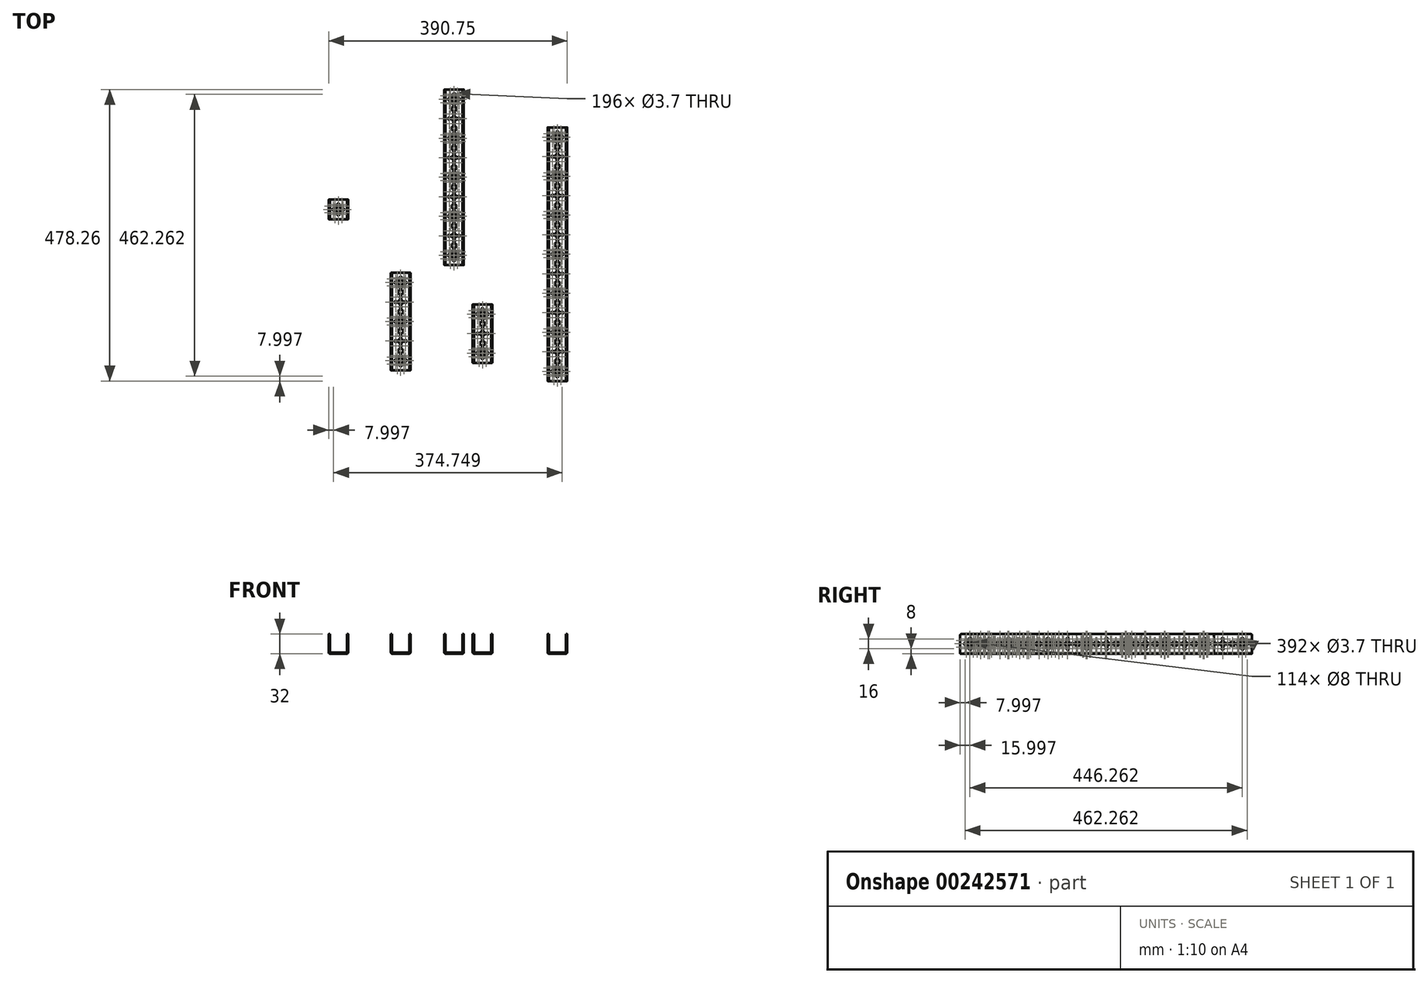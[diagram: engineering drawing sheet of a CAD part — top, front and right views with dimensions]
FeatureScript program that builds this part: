
annotation { "Feature Type Name" : "Feature", "Feature Type Description" : "" }
export const myFeature = defineFeature(function(context is Context, id is Id, definition is map)
    precondition{}
    {
        {
            var Q0;
            Q0=qCreatedBy(makeId("Top.planeOp"),FACE);
            var sketch = newSketch(context, id + "F0", { "sketchPlane" : qUnion([Q0])});
            skLineSegment(sketch, "E0.bottom", {"start": v(-59.46, 42.92) * mm, "end": v(-27.46, 42.92) * mm});
            skLineSegment(sketch, "E0.top", {"start": v(-59.46, -53.08) * mm, "end": v(-27.46, -53.08) * mm});
            skLineSegment(sketch, "E0.left", {"start": v(-59.46, 42.92) * mm, "end": v(-59.46, -53.08) * mm});
            skLineSegment(sketch, "E0.right", {"start": v(-27.46, 42.92) * mm, "end": v(-27.46, -53.08) * mm});
            skCircle(sketch, "E1", {"center": v(-43.46, 26.92) * mm, "radius": 4 * mm});
            skCircle(sketch, "E2.0.1.0", {"center": v(-43.46, 10.92) * mm, "radius": 4 * mm});
            skCircle(sketch, "E2.0.2.0", {"center": v(-43.46, -5.08) * mm, "radius": 4 * mm});
            skCircle(sketch, "E2.0.3.0", {"center": v(-43.46, -21.08) * mm, "radius": 4 * mm});
            skCircle(sketch, "E2.0.4.0", {"center": v(-43.46, -37.08) * mm, "radius": 4 * mm});
            skLineSegment(sketch, "E2.direction1", {"start": v(-43.46, 26.92) * mm, "end": v(4.3, 26.92) * mm, "construction": true});
            skLineSegment(sketch, "E2.direction2", {"start": v(-43.46, 26.92) * mm, "end": v(-43.46, 10.92) * mm, "construction": true});
            skCircle(sketch, "E3", {"center": v(-43.46, 34.92) * mm, "radius": 1.85 * mm});
            skCircle(sketch, "E4.1.0", {"center": v(-49.12, 32.57) * mm, "radius": 1.85 * mm});
            skCircle(sketch, "E4.2.0", {"center": v(-51.46, 26.92) * mm, "radius": 1.85 * mm});
            skCircle(sketch, "E4.3.0", {"center": v(-49.12, 21.26) * mm, "radius": 1.85 * mm});
            skCircle(sketch, "E4.4.0", {"center": v(-43.46, 18.92) * mm, "radius": 1.85 * mm});
            skCircle(sketch, "E4.5.0", {"center": v(-37.8, 21.26) * mm, "radius": 1.85 * mm});
            skCircle(sketch, "E4.6.0", {"center": v(-35.46, 26.92) * mm, "radius": 1.85 * mm});
            skCircle(sketch, "E4.7.0", {"center": v(-37.8, 32.57) * mm, "radius": 1.85 * mm});
            skCircle(sketch, "E5.0.1.0", {"center": v(-43.46, -13.08) * mm, "radius": 1.85 * mm});
            skCircle(sketch, "E5.0.1.1", {"center": v(-51.46, -5.08) * mm, "radius": 1.85 * mm});
            skCircle(sketch, "E5.0.1.2", {"center": v(-43.46, 2.92) * mm, "radius": 1.85 * mm});
            skCircle(sketch, "E5.0.1.3", {"center": v(-35.46, -5.08) * mm, "radius": 1.85 * mm});
            skCircle(sketch, "E5.0.2.0", {"center": v(-43.46, -45.08) * mm, "radius": 1.85 * mm});
            skCircle(sketch, "E5.0.2.1", {"center": v(-51.46, -37.08) * mm, "radius": 1.85 * mm});
            skCircle(sketch, "E5.0.2.2", {"center": v(-43.46, -29.08) * mm, "radius": 1.85 * mm});
            skCircle(sketch, "E5.0.2.3", {"center": v(-35.46, -37.08) * mm, "radius": 1.85 * mm});
            skCircle(sketch, "E5.0.2.4", {"center": v(-37.8, -42.74) * mm, "radius": 1.85 * mm});
            skCircle(sketch, "E5.0.2.5", {"center": v(-49.12, -42.74) * mm, "radius": 1.85 * mm});
            skCircle(sketch, "E5.0.2.6", {"center": v(-49.12, -31.43) * mm, "radius": 1.85 * mm});
            skCircle(sketch, "E5.0.2.7", {"center": v(-37.8, -31.43) * mm, "radius": 1.85 * mm});
            skLineSegment(sketch, "E5.direction1", {"start": v(-43.46, 18.92) * mm, "end": v(-18.06, 18.92) * mm, "construction": true});
            skLineSegment(sketch, "E5.direction2", {"start": v(-43.46, 18.92) * mm, "end": v(-43.46, -13.08) * mm, "construction": true});
            skLineSegment(sketch, "E6.bottom", {"start": v(63.23, 333.14) * mm, "end": v(95.23, 333.14) * mm});
            skLineSegment(sketch, "E6.top", {"start": v(63.23, -82.86) * mm, "end": v(95.23, -82.86) * mm});
            skLineSegment(sketch, "E6.left", {"start": v(63.23, 333.14) * mm, "end": v(63.23, -82.86) * mm});
            skLineSegment(sketch, "E6.right", {"start": v(95.23, 333.14) * mm, "end": v(95.23, -82.86) * mm});
            skCircle(sketch, "E7", {"center": v(79.23, -66.86) * mm, "radius": 4 * mm});
            skCircle(sketch, "E8.0.1.0", {"center": v(79.23, -50.86) * mm, "radius": 4 * mm});
            skCircle(sketch, "E8.0.2.0", {"center": v(79.23, -34.86) * mm, "radius": 4 * mm});
            skCircle(sketch, "E8.0.3.0", {"center": v(79.23, -18.86) * mm, "radius": 4 * mm});
            skCircle(sketch, "E8.0.4.0", {"center": v(79.23, -2.86) * mm, "radius": 4 * mm});
            skCircle(sketch, "E8.0.5.0", {"center": v(79.23, 13.14) * mm, "radius": 4 * mm});
            skCircle(sketch, "E8.0.6.0", {"center": v(79.23, 29.14) * mm, "radius": 4 * mm});
            skCircle(sketch, "E8.0.7.0", {"center": v(79.23, 45.14) * mm, "radius": 4 * mm});
            skCircle(sketch, "E8.0.8.0", {"center": v(79.23, 61.14) * mm, "radius": 4 * mm});
            skCircle(sketch, "E8.0.9.0", {"center": v(79.23, 77.14) * mm, "radius": 4 * mm});
            skCircle(sketch, "E8.0.10.0", {"center": v(79.23, 93.14) * mm, "radius": 4 * mm});
            skCircle(sketch, "E8.0.11.0", {"center": v(79.23, 109.14) * mm, "radius": 4 * mm});
            skCircle(sketch, "E8.0.12.0", {"center": v(79.23, 125.14) * mm, "radius": 4 * mm});
            skCircle(sketch, "E8.0.13.0", {"center": v(79.23, 141.14) * mm, "radius": 4 * mm});
            skCircle(sketch, "E8.0.14.0", {"center": v(79.23, 157.14) * mm, "radius": 4 * mm});
            skCircle(sketch, "E8.0.15.0", {"center": v(79.23, 173.14) * mm, "radius": 4 * mm});
            skCircle(sketch, "E8.0.16.0", {"center": v(79.23, 189.14) * mm, "radius": 4 * mm});
            skCircle(sketch, "E8.0.17.0", {"center": v(79.23, 205.14) * mm, "radius": 4 * mm});
            skCircle(sketch, "E8.0.18.0", {"center": v(79.23, 221.14) * mm, "radius": 4 * mm});
            skCircle(sketch, "E8.0.19.0", {"center": v(79.23, 237.14) * mm, "radius": 4 * mm});
            skCircle(sketch, "E8.0.20.0", {"center": v(79.23, 253.14) * mm, "radius": 4 * mm});
            skCircle(sketch, "E8.0.21.0", {"center": v(79.23, 269.14) * mm, "radius": 4 * mm});
            skCircle(sketch, "E8.0.22.0", {"center": v(79.23, 285.14) * mm, "radius": 4 * mm});
            skCircle(sketch, "E8.0.23.0", {"center": v(79.23, 301.14) * mm, "radius": 4 * mm});
            skCircle(sketch, "E8.0.24.0", {"center": v(79.23, 317.14) * mm, "radius": 4 * mm});
            skLineSegment(sketch, "E8.direction1", {"start": v(79.23, -66.86) * mm, "end": v(104.63, -66.86) * mm, "construction": true});
            skLineSegment(sketch, "E8.direction2", {"start": v(79.23, -66.86) * mm, "end": v(79.23, -50.86) * mm, "construction": true});
            skCircle(sketch, "E9", {"center": v(79.23, -74.86) * mm, "radius": 1.85 * mm});
            skCircle(sketch, "E10.1.0", {"center": v(84.88, -72.52) * mm, "radius": 1.85 * mm});
            skCircle(sketch, "E10.2.0", {"center": v(87.23, -66.86) * mm, "radius": 1.85 * mm});
            skCircle(sketch, "E10.3.0", {"center": v(84.88, -61.2) * mm, "radius": 1.85 * mm});
            skCircle(sketch, "E10.4.0", {"center": v(79.23, -58.86) * mm, "radius": 1.85 * mm});
            skCircle(sketch, "E10.5.0", {"center": v(73.57, -61.2) * mm, "radius": 1.85 * mm});
            skCircle(sketch, "E10.6.0", {"center": v(71.23, -66.86) * mm, "radius": 1.85 * mm});
            skCircle(sketch, "E10.7.0", {"center": v(73.57, -72.52) * mm, "radius": 1.85 * mm});
            skCircle(sketch, "E11.0.1.0", {"center": v(79.23, -26.86) * mm, "radius": 1.85 * mm});
            skCircle(sketch, "E11.0.1.2", {"center": v(71.23, -34.86) * mm, "radius": 1.85 * mm});
            skCircle(sketch, "E11.0.1.4", {"center": v(79.23, -42.86) * mm, "radius": 1.85 * mm});
            skCircle(sketch, "E11.0.1.6", {"center": v(87.23, -34.86) * mm, "radius": 1.85 * mm});
            skCircle(sketch, "E11.0.2.0", {"center": v(79.23, 5.14) * mm, "radius": 1.85 * mm});
            skCircle(sketch, "E11.0.2.1", {"center": v(73.57, 2.8) * mm, "radius": 1.85 * mm});
            skCircle(sketch, "E11.0.2.2", {"center": v(71.23, -2.86) * mm, "radius": 1.85 * mm});
            skCircle(sketch, "E11.0.2.3", {"center": v(73.57, -8.52) * mm, "radius": 1.85 * mm});
            skCircle(sketch, "E11.0.2.4", {"center": v(79.23, -10.86) * mm, "radius": 1.85 * mm});
            skCircle(sketch, "E11.0.2.5", {"center": v(84.88, -8.52) * mm, "radius": 1.85 * mm});
            skCircle(sketch, "E11.0.2.6", {"center": v(87.23, -2.86) * mm, "radius": 1.85 * mm});
            skCircle(sketch, "E11.0.2.7", {"center": v(84.88, 2.8) * mm, "radius": 1.85 * mm});
            skCircle(sketch, "E11.0.3.0", {"center": v(79.23, 37.14) * mm, "radius": 1.85 * mm});
            skCircle(sketch, "E11.0.3.2", {"center": v(71.23, 29.14) * mm, "radius": 1.85 * mm});
            skCircle(sketch, "E11.0.3.4", {"center": v(79.23, 21.14) * mm, "radius": 1.85 * mm});
            skCircle(sketch, "E11.0.3.6", {"center": v(87.23, 29.14) * mm, "radius": 1.85 * mm});
            skCircle(sketch, "E11.0.4.0", {"center": v(79.23, 69.14) * mm, "radius": 1.85 * mm});
            skCircle(sketch, "E11.0.4.1", {"center": v(73.57, 66.8) * mm, "radius": 1.85 * mm});
            skCircle(sketch, "E11.0.4.2", {"center": v(71.23, 61.14) * mm, "radius": 1.85 * mm});
            skCircle(sketch, "E11.0.4.3", {"center": v(73.57, 55.48) * mm, "radius": 1.85 * mm});
            skCircle(sketch, "E11.0.4.4", {"center": v(79.23, 53.14) * mm, "radius": 1.85 * mm});
            skCircle(sketch, "E11.0.4.5", {"center": v(84.88, 55.48) * mm, "radius": 1.85 * mm});
            skCircle(sketch, "E11.0.4.6", {"center": v(87.23, 61.14) * mm, "radius": 1.85 * mm});
            skCircle(sketch, "E11.0.4.7", {"center": v(84.88, 66.8) * mm, "radius": 1.85 * mm});
            skCircle(sketch, "E11.0.5.0", {"center": v(79.23, 101.14) * mm, "radius": 1.85 * mm});
            skCircle(sketch, "E11.0.5.2", {"center": v(71.23, 93.14) * mm, "radius": 1.85 * mm});
            skCircle(sketch, "E11.0.5.4", {"center": v(79.23, 85.14) * mm, "radius": 1.85 * mm});
            skCircle(sketch, "E11.0.5.6", {"center": v(87.23, 93.14) * mm, "radius": 1.85 * mm});
            skCircle(sketch, "E11.0.6.0", {"center": v(79.23, 133.14) * mm, "radius": 1.85 * mm});
            skCircle(sketch, "E11.0.6.1", {"center": v(73.57, 130.8) * mm, "radius": 1.85 * mm});
            skCircle(sketch, "E11.0.6.2", {"center": v(71.23, 125.14) * mm, "radius": 1.85 * mm});
            skCircle(sketch, "E11.0.6.3", {"center": v(73.57, 119.48) * mm, "radius": 1.85 * mm});
            skCircle(sketch, "E11.0.6.4", {"center": v(79.23, 117.14) * mm, "radius": 1.85 * mm});
            skCircle(sketch, "E11.0.6.5", {"center": v(84.88, 119.48) * mm, "radius": 1.85 * mm});
            skCircle(sketch, "E11.0.6.6", {"center": v(87.23, 125.14) * mm, "radius": 1.85 * mm});
            skCircle(sketch, "E11.0.6.7", {"center": v(84.88, 130.8) * mm, "radius": 1.85 * mm});
            skCircle(sketch, "E11.0.7.0", {"center": v(79.23, 165.14) * mm, "radius": 1.85 * mm});
            skCircle(sketch, "E11.0.7.2", {"center": v(71.23, 157.14) * mm, "radius": 1.85 * mm});
            skCircle(sketch, "E11.0.7.4", {"center": v(79.23, 149.14) * mm, "radius": 1.85 * mm});
            skCircle(sketch, "E11.0.7.6", {"center": v(87.23, 157.14) * mm, "radius": 1.85 * mm});
            skCircle(sketch, "E11.0.8.0", {"center": v(79.23, 197.14) * mm, "radius": 1.85 * mm});
            skCircle(sketch, "E11.0.8.1", {"center": v(73.57, 194.8) * mm, "radius": 1.85 * mm});
            skCircle(sketch, "E11.0.8.2", {"center": v(71.23, 189.14) * mm, "radius": 1.85 * mm});
            skCircle(sketch, "E11.0.8.3", {"center": v(73.57, 183.48) * mm, "radius": 1.85 * mm});
            skCircle(sketch, "E11.0.8.4", {"center": v(79.23, 181.14) * mm, "radius": 1.85 * mm});
            skCircle(sketch, "E11.0.8.5", {"center": v(84.88, 183.48) * mm, "radius": 1.85 * mm});
            skCircle(sketch, "E11.0.8.6", {"center": v(87.23, 189.14) * mm, "radius": 1.85 * mm});
            skCircle(sketch, "E11.0.8.7", {"center": v(84.88, 194.8) * mm, "radius": 1.85 * mm});
            skCircle(sketch, "E11.0.9.0", {"center": v(79.23, 229.14) * mm, "radius": 1.85 * mm});
            skCircle(sketch, "E11.0.9.2", {"center": v(71.23, 221.14) * mm, "radius": 1.85 * mm});
            skCircle(sketch, "E11.0.9.4", {"center": v(79.23, 213.14) * mm, "radius": 1.85 * mm});
            skCircle(sketch, "E11.0.9.6", {"center": v(87.23, 221.14) * mm, "radius": 1.85 * mm});
            skCircle(sketch, "E11.0.10.0", {"center": v(79.23, 261.14) * mm, "radius": 1.85 * mm});
            skCircle(sketch, "E11.0.10.1", {"center": v(73.57, 258.8) * mm, "radius": 1.85 * mm});
            skCircle(sketch, "E11.0.10.2", {"center": v(71.23, 253.14) * mm, "radius": 1.85 * mm});
            skCircle(sketch, "E11.0.10.3", {"center": v(73.57, 247.48) * mm, "radius": 1.85 * mm});
            skCircle(sketch, "E11.0.10.4", {"center": v(79.23, 245.14) * mm, "radius": 1.85 * mm});
            skCircle(sketch, "E11.0.10.5", {"center": v(84.88, 247.48) * mm, "radius": 1.85 * mm});
            skCircle(sketch, "E11.0.10.6", {"center": v(87.23, 253.14) * mm, "radius": 1.85 * mm});
            skCircle(sketch, "E11.0.10.7", {"center": v(84.88, 258.8) * mm, "radius": 1.85 * mm});
            skCircle(sketch, "E11.0.11.0", {"center": v(79.23, 293.14) * mm, "radius": 1.85 * mm});
            skCircle(sketch, "E11.0.11.2", {"center": v(71.23, 285.14) * mm, "radius": 1.85 * mm});
            skCircle(sketch, "E11.0.11.4", {"center": v(79.23, 277.14) * mm, "radius": 1.85 * mm});
            skCircle(sketch, "E11.0.11.6", {"center": v(87.23, 285.14) * mm, "radius": 1.85 * mm});
            skCircle(sketch, "E11.0.12.0", {"center": v(79.23, 325.14) * mm, "radius": 1.85 * mm});
            skCircle(sketch, "E11.0.12.1", {"center": v(73.57, 322.8) * mm, "radius": 1.85 * mm});
            skCircle(sketch, "E11.0.12.2", {"center": v(71.23, 317.14) * mm, "radius": 1.85 * mm});
            skCircle(sketch, "E11.0.12.3", {"center": v(73.57, 311.48) * mm, "radius": 1.85 * mm});
            skCircle(sketch, "E11.0.12.4", {"center": v(79.23, 309.14) * mm, "radius": 1.85 * mm});
            skCircle(sketch, "E11.0.12.5", {"center": v(84.88, 311.48) * mm, "radius": 1.85 * mm});
            skCircle(sketch, "E11.0.12.6", {"center": v(87.23, 317.14) * mm, "radius": 1.85 * mm});
            skCircle(sketch, "E11.0.12.7", {"center": v(84.88, 322.8) * mm, "radius": 1.85 * mm});
            skLineSegment(sketch, "E11.direction1", {"start": v(79.23, -58.86) * mm, "end": v(125.96, -58.86) * mm, "construction": true});
            skLineSegment(sketch, "E11.direction2", {"start": v(79.23, -58.86) * mm, "end": v(79.23, -26.86) * mm, "construction": true});
            skLineSegment(sketch, "E12.bottom", {"start": v(-193.52, 94.72) * mm, "end": v(-161.52, 94.72) * mm});
            skLineSegment(sketch, "E12.top", {"start": v(-193.52, -65.28) * mm, "end": v(-161.52, -65.28) * mm});
            skLineSegment(sketch, "E12.left", {"start": v(-193.52, 94.72) * mm, "end": v(-193.52, -65.28) * mm});
            skLineSegment(sketch, "E12.right", {"start": v(-161.52, 94.72) * mm, "end": v(-161.52, -65.28) * mm});
            skCircle(sketch, "E13", {"center": v(-177.52, 78.72) * mm, "radius": 4 * mm});
            skCircle(sketch, "E14", {"center": v(-177.52, 86.72) * mm, "radius": 1.85 * mm});
            skCircle(sketch, "E15.1.0", {"center": v(-183.18, 84.38) * mm, "radius": 1.85 * mm});
            skCircle(sketch, "E15.2.0", {"center": v(-185.52, 78.72) * mm, "radius": 1.85 * mm});
            skCircle(sketch, "E15.3.0", {"center": v(-183.18, 73.07) * mm, "radius": 1.85 * mm});
            skCircle(sketch, "E15.4.0", {"center": v(-177.52, 70.72) * mm, "radius": 1.85 * mm});
            skCircle(sketch, "E15.5.0", {"center": v(-171.86, 73.07) * mm, "radius": 1.85 * mm});
            skCircle(sketch, "E15.6.0", {"center": v(-169.52, 78.72) * mm, "radius": 1.85 * mm});
            skCircle(sketch, "E15.7.0", {"center": v(-171.86, 84.38) * mm, "radius": 1.85 * mm});
            skCircle(sketch, "E16.0.1.0", {"center": v(-177.52, 38.72) * mm, "radius": 1.85 * mm});
            skCircle(sketch, "E16.0.1.2", {"center": v(-177.52, 46.72) * mm, "radius": 4 * mm});
            skCircle(sketch, "E16.0.1.3", {"center": v(-185.52, 46.72) * mm, "radius": 1.85 * mm});
            skCircle(sketch, "E16.0.1.5", {"center": v(-177.52, 54.72) * mm, "radius": 1.85 * mm});
            skCircle(sketch, "E16.0.1.7", {"center": v(-169.52, 46.72) * mm, "radius": 1.85 * mm});
            skCircle(sketch, "E16.0.2.0", {"center": v(-177.52, 6.72) * mm, "radius": 1.85 * mm});
            skCircle(sketch, "E16.0.2.1", {"center": v(-183.18, 9.07) * mm, "radius": 1.85 * mm});
            skCircle(sketch, "E16.0.2.2", {"center": v(-177.52, 14.72) * mm, "radius": 4 * mm});
            skCircle(sketch, "E16.0.2.3", {"center": v(-185.52, 14.72) * mm, "radius": 1.85 * mm});
            skCircle(sketch, "E16.0.2.4", {"center": v(-183.18, 20.38) * mm, "radius": 1.85 * mm});
            skCircle(sketch, "E16.0.2.5", {"center": v(-177.52, 22.72) * mm, "radius": 1.85 * mm});
            skCircle(sketch, "E16.0.2.6", {"center": v(-171.86, 20.38) * mm, "radius": 1.85 * mm});
            skCircle(sketch, "E16.0.2.7", {"center": v(-169.52, 14.72) * mm, "radius": 1.85 * mm});
            skCircle(sketch, "E16.0.2.8", {"center": v(-171.86, 9.07) * mm, "radius": 1.85 * mm});
            skCircle(sketch, "E16.0.3.0", {"center": v(-177.52, -25.28) * mm, "radius": 1.85 * mm});
            skCircle(sketch, "E16.0.3.2", {"center": v(-177.52, -17.28) * mm, "radius": 4 * mm});
            skCircle(sketch, "E16.0.3.3", {"center": v(-185.52, -17.28) * mm, "radius": 1.85 * mm});
            skCircle(sketch, "E16.0.3.5", {"center": v(-177.52, -9.28) * mm, "radius": 1.85 * mm});
            skCircle(sketch, "E16.0.3.7", {"center": v(-169.52, -17.28) * mm, "radius": 1.85 * mm});
            skCircle(sketch, "E16.0.4.0", {"center": v(-177.52, -57.28) * mm, "radius": 1.85 * mm});
            skCircle(sketch, "E16.0.4.1", {"center": v(-183.18, -54.93) * mm, "radius": 1.85 * mm});
            skCircle(sketch, "E16.0.4.2", {"center": v(-177.52, -49.28) * mm, "radius": 4 * mm});
            skCircle(sketch, "E16.0.4.3", {"center": v(-185.52, -49.28) * mm, "radius": 1.85 * mm});
            skCircle(sketch, "E16.0.4.4", {"center": v(-183.18, -43.62) * mm, "radius": 1.85 * mm});
            skCircle(sketch, "E16.0.4.5", {"center": v(-177.52, -41.28) * mm, "radius": 1.85 * mm});
            skCircle(sketch, "E16.0.4.6", {"center": v(-171.86, -43.62) * mm, "radius": 1.85 * mm});
            skCircle(sketch, "E16.0.4.7", {"center": v(-169.52, -49.28) * mm, "radius": 1.85 * mm});
            skCircle(sketch, "E16.0.4.8", {"center": v(-171.86, -54.93) * mm, "radius": 1.85 * mm});
            skLineSegment(sketch, "E16.direction1", {"start": v(-177.52, 70.72) * mm, "end": v(-152.12, 70.72) * mm, "construction": true});
            skLineSegment(sketch, "E16.direction2", {"start": v(-177.52, 70.72) * mm, "end": v(-177.52, 38.72) * mm, "construction": true});
            skCircle(sketch, "E17.0.1.0", {"center": v(-177.52, 62.72) * mm, "radius": 4 * mm});
            skCircle(sketch, "E17.0.1.1", {"center": v(-177.52, 30.72) * mm, "radius": 4 * mm});
            skCircle(sketch, "E17.0.1.2", {"center": v(-177.52, -1.28) * mm, "radius": 4 * mm});
            skCircle(sketch, "E17.0.1.3", {"center": v(-177.52, -33.28) * mm, "radius": 4 * mm});
            skLineSegment(sketch, "E17.direction1", {"start": v(-177.52, 78.72) * mm, "end": v(-152.12, 78.72) * mm, "construction": true});
            skLineSegment(sketch, "E17.direction2", {"start": v(-177.52, 78.72) * mm, "end": v(-177.52, 62.72) * mm, "construction": true});
            skLineSegment(sketch, "E18.bottom", {"start": v(-106.07, 395.4) * mm, "end": v(-74.07, 395.4) * mm});
            skLineSegment(sketch, "E18.top", {"start": v(-106.07, 107.4) * mm, "end": v(-74.07, 107.4) * mm});
            skLineSegment(sketch, "E18.left", {"start": v(-106.07, 395.4) * mm, "end": v(-106.07, 107.4) * mm});
            skLineSegment(sketch, "E18.right", {"start": v(-74.07, 395.4) * mm, "end": v(-74.07, 107.4) * mm});
            skCircle(sketch, "E19", {"center": v(-90.07, 123.4) * mm, "radius": 4 * mm});
            skCircle(sketch, "E20", {"center": v(-90.07, 115.4) * mm, "radius": 1.85 * mm});
            skCircle(sketch, "E21.1.0", {"center": v(-84.41, 117.74) * mm, "radius": 1.85 * mm});
            skCircle(sketch, "E21.2.0", {"center": v(-82.07, 123.4) * mm, "radius": 1.85 * mm});
            skCircle(sketch, "E21.3.0", {"center": v(-84.41, 129.06) * mm, "radius": 1.85 * mm});
            skCircle(sketch, "E21.4.0", {"center": v(-90.07, 131.4) * mm, "radius": 1.85 * mm});
            skCircle(sketch, "E21.5.0", {"center": v(-95.73, 129.06) * mm, "radius": 1.85 * mm});
            skCircle(sketch, "E21.6.0", {"center": v(-98.07, 123.4) * mm, "radius": 1.85 * mm});
            skCircle(sketch, "E21.7.0", {"center": v(-95.73, 117.74) * mm, "radius": 1.85 * mm});
            skCircle(sketch, "E22.0.1.0", {"center": v(-82.07, 155.4) * mm, "radius": 1.85 * mm});
            skCircle(sketch, "E22.0.1.1", {"center": v(-90.07, 155.4) * mm, "radius": 4 * mm});
            skCircle(sketch, "E22.0.1.3", {"center": v(-90.07, 147.4) * mm, "radius": 1.85 * mm});
            skCircle(sketch, "E22.0.1.5", {"center": v(-98.07, 155.4) * mm, "radius": 1.85 * mm});
            skCircle(sketch, "E22.0.1.7", {"center": v(-90.07, 163.4) * mm, "radius": 1.85 * mm});
            skCircle(sketch, "E22.0.2.0", {"center": v(-82.07, 187.4) * mm, "radius": 1.85 * mm});
            skCircle(sketch, "E22.0.2.1", {"center": v(-90.07, 187.4) * mm, "radius": 4 * mm});
            skCircle(sketch, "E22.0.2.2", {"center": v(-84.41, 181.74) * mm, "radius": 1.85 * mm});
            skCircle(sketch, "E22.0.2.3", {"center": v(-90.07, 179.4) * mm, "radius": 1.85 * mm});
            skCircle(sketch, "E22.0.2.4", {"center": v(-95.73, 181.74) * mm, "radius": 1.85 * mm});
            skCircle(sketch, "E22.0.2.5", {"center": v(-98.07, 187.4) * mm, "radius": 1.85 * mm});
            skCircle(sketch, "E22.0.2.6", {"center": v(-95.73, 193.06) * mm, "radius": 1.85 * mm});
            skCircle(sketch, "E22.0.2.7", {"center": v(-90.07, 195.4) * mm, "radius": 1.85 * mm});
            skCircle(sketch, "E22.0.2.8", {"center": v(-84.41, 193.06) * mm, "radius": 1.85 * mm});
            skCircle(sketch, "E22.0.3.0", {"center": v(-82.07, 219.4) * mm, "radius": 1.85 * mm});
            skCircle(sketch, "E22.0.3.1", {"center": v(-90.07, 219.4) * mm, "radius": 4 * mm});
            skCircle(sketch, "E22.0.3.3", {"center": v(-90.07, 211.4) * mm, "radius": 1.85 * mm});
            skCircle(sketch, "E22.0.3.5", {"center": v(-98.07, 219.4) * mm, "radius": 1.85 * mm});
            skCircle(sketch, "E22.0.3.7", {"center": v(-90.07, 227.4) * mm, "radius": 1.85 * mm});
            skCircle(sketch, "E22.0.4.0", {"center": v(-82.07, 251.4) * mm, "radius": 1.85 * mm});
            skCircle(sketch, "E22.0.4.1", {"center": v(-90.07, 251.4) * mm, "radius": 4 * mm});
            skCircle(sketch, "E22.0.4.2", {"center": v(-84.41, 245.74) * mm, "radius": 1.85 * mm});
            skCircle(sketch, "E22.0.4.3", {"center": v(-90.07, 243.4) * mm, "radius": 1.85 * mm});
            skCircle(sketch, "E22.0.4.4", {"center": v(-95.73, 245.74) * mm, "radius": 1.85 * mm});
            skCircle(sketch, "E22.0.4.5", {"center": v(-98.07, 251.4) * mm, "radius": 1.85 * mm});
            skCircle(sketch, "E22.0.4.6", {"center": v(-95.73, 257.06) * mm, "radius": 1.85 * mm});
            skCircle(sketch, "E22.0.4.7", {"center": v(-90.07, 259.4) * mm, "radius": 1.85 * mm});
            skCircle(sketch, "E22.0.4.8", {"center": v(-84.41, 257.06) * mm, "radius": 1.85 * mm});
            skCircle(sketch, "E22.0.5.0", {"center": v(-82.07, 283.4) * mm, "radius": 1.85 * mm});
            skCircle(sketch, "E22.0.5.1", {"center": v(-90.07, 283.4) * mm, "radius": 4 * mm});
            skCircle(sketch, "E22.0.5.3", {"center": v(-90.07, 275.4) * mm, "radius": 1.85 * mm});
            skCircle(sketch, "E22.0.5.5", {"center": v(-98.07, 283.4) * mm, "radius": 1.85 * mm});
            skCircle(sketch, "E22.0.5.7", {"center": v(-90.07, 291.4) * mm, "radius": 1.85 * mm});
            skCircle(sketch, "E22.0.6.0", {"center": v(-82.07, 315.4) * mm, "radius": 1.85 * mm});
            skCircle(sketch, "E22.0.6.1", {"center": v(-90.07, 315.4) * mm, "radius": 4 * mm});
            skCircle(sketch, "E22.0.6.2", {"center": v(-84.41, 309.74) * mm, "radius": 1.85 * mm});
            skCircle(sketch, "E22.0.6.3", {"center": v(-90.07, 307.4) * mm, "radius": 1.85 * mm});
            skCircle(sketch, "E22.0.6.4", {"center": v(-95.73, 309.74) * mm, "radius": 1.85 * mm});
            skCircle(sketch, "E22.0.6.5", {"center": v(-98.07, 315.4) * mm, "radius": 1.85 * mm});
            skCircle(sketch, "E22.0.6.6", {"center": v(-95.73, 321.06) * mm, "radius": 1.85 * mm});
            skCircle(sketch, "E22.0.6.7", {"center": v(-90.07, 323.4) * mm, "radius": 1.85 * mm});
            skCircle(sketch, "E22.0.6.8", {"center": v(-84.41, 321.06) * mm, "radius": 1.85 * mm});
            skLineSegment(sketch, "E22.direction1", {"start": v(-82.07, 123.4) * mm, "end": v(-56.67, 123.4) * mm, "construction": true});
            skLineSegment(sketch, "E22.direction2", {"start": v(-82.07, 123.4) * mm, "end": v(-82.07, 155.4) * mm, "construction": true});
            skCircle(sketch, "E23.0.1.0", {"center": v(-90.07, 203.4) * mm, "radius": 4 * mm});
            skCircle(sketch, "E23.0.1.1", {"center": v(-90.07, 171.4) * mm, "radius": 4 * mm});
            skCircle(sketch, "E23.0.1.2", {"center": v(-90.07, 139.4) * mm, "radius": 4 * mm});
            skCircle(sketch, "E23.0.1.4", {"center": v(-90.07, 299.4) * mm, "radius": 4 * mm});
            skCircle(sketch, "E23.0.1.5", {"center": v(-90.07, 267.4) * mm, "radius": 4 * mm});
            skCircle(sketch, "E23.0.1.6", {"center": v(-90.07, 235.4) * mm, "radius": 4 * mm});
            skLineSegment(sketch, "E23.direction1", {"start": v(-90.07, 187.4) * mm, "end": v(-64.67, 187.4) * mm, "construction": true});
            skLineSegment(sketch, "E23.direction2", {"start": v(-90.07, 187.4) * mm, "end": v(-90.07, 203.4) * mm, "construction": true});
            skCircle(sketch, "E24.0.0.7", {"center": v(-82.07, 347.4) * mm, "radius": 1.85 * mm});
            skCircle(sketch, "E24.2.0.7", {"center": v(-90.07, 347.4) * mm, "radius": 4 * mm});
            skCircle(sketch, "E24.6.0.7", {"center": v(-90.07, 339.4) * mm, "radius": 1.85 * mm});
            skCircle(sketch, "E24.10.0.7", {"center": v(-98.07, 347.4) * mm, "radius": 1.85 * mm});
            skCircle(sketch, "E24.14.0.7", {"center": v(-90.07, 355.4) * mm, "radius": 1.85 * mm});
            skCircle(sketch, "E24.0.0.8", {"center": v(-82.07, 379.4) * mm, "radius": 1.85 * mm});
            skCircle(sketch, "E24.2.0.8", {"center": v(-90.07, 379.4) * mm, "radius": 4 * mm});
            skCircle(sketch, "E24.4.0.8", {"center": v(-84.41, 373.74) * mm, "radius": 1.85 * mm});
            skCircle(sketch, "E24.6.0.8", {"center": v(-90.07, 371.4) * mm, "radius": 1.85 * mm});
            skCircle(sketch, "E24.8.0.8", {"center": v(-95.73, 373.74) * mm, "radius": 1.85 * mm});
            skCircle(sketch, "E24.10.0.8", {"center": v(-98.07, 379.4) * mm, "radius": 1.85 * mm});
            skCircle(sketch, "E24.12.0.8", {"center": v(-95.73, 385.06) * mm, "radius": 1.85 * mm});
            skCircle(sketch, "E24.14.0.8", {"center": v(-90.07, 387.4) * mm, "radius": 1.85 * mm});
            skCircle(sketch, "E24.16.0.8", {"center": v(-84.41, 385.06) * mm, "radius": 1.85 * mm});
            skCircle(sketch, "E25.0.1.0", {"center": v(-90.07, 363.4) * mm, "radius": 4 * mm});
            skCircle(sketch, "E25.0.1.1", {"center": v(-90.07, 331.4) * mm, "radius": 4 * mm});
            skLineSegment(sketch, "E25.direction1", {"start": v(-90.07, 315.4) * mm, "end": v(-64.67, 315.4) * mm, "construction": true});
            skLineSegment(sketch, "E25.direction2", {"start": v(-90.07, 315.4) * mm, "end": v(-90.07, 331.4) * mm, "construction": true});
            skSolve(sketch);
        }
        {
            var Q0;
            Q0 = qSketchRegion(id + "F0", true);
            extrude(context, id + "F1", {"entities" : qUnion([Q0]), "depth" : 32 * mm});
        }
        {
            var Q0;
            Q0=makeQuery(id+"F1.opExtrude","SWEPT_FACE",FACE,{"disambiguationData":[OSD([sQuery(id+"F0.wireOp",EDGE,"E0.right")])]});
            var sketch = newSketch(context, id + "F2", { "sketchPlane" : qUnion([Q0])});
            skCircle(sketch, "E26", {"center": v(-37.08, 16) * mm, "radius": 4 * mm});
            skCircle(sketch, "E27", {"center": v(-45.08, 16) * mm, "radius": 1.85 * mm});
            skPoint(sketch, "E27.centerSnap0", {"position": v(-53.08, 16) * mm});
            skCircle(sketch, "E28.1.0", {"center": v(-42.74, 10.34) * mm, "radius": 1.85 * mm});
            skCircle(sketch, "E28.2.0", {"center": v(-37.08, 8) * mm, "radius": 1.85 * mm});
            skCircle(sketch, "E28.3.0", {"center": v(-31.43, 10.34) * mm, "radius": 1.85 * mm});
            skCircle(sketch, "E28.4.0", {"center": v(-29.08, 16) * mm, "radius": 1.85 * mm});
            skCircle(sketch, "E28.5.0", {"center": v(-31.43, 21.66) * mm, "radius": 1.85 * mm});
            skCircle(sketch, "E28.6.0", {"center": v(-37.08, 24) * mm, "radius": 1.85 * mm});
            skCircle(sketch, "E28.7.0", {"center": v(-42.74, 21.66) * mm, "radius": 1.85 * mm});
            skCircle(sketch, "E29.1.0.0", {"center": v(2.92, 16) * mm, "radius": 1.85 * mm});
            skCircle(sketch, "E29.1.0.2", {"center": v(-5.08, 8) * mm, "radius": 1.85 * mm});
            skCircle(sketch, "E29.1.0.4", {"center": v(-13.08, 16) * mm, "radius": 1.85 * mm});
            skCircle(sketch, "E29.1.0.6", {"center": v(-5.08, 24) * mm, "radius": 1.85 * mm});
            skCircle(sketch, "E29.2.0.0", {"center": v(34.92, 16) * mm, "radius": 1.85 * mm});
            skCircle(sketch, "E29.2.0.1", {"center": v(32.57, 10.34) * mm, "radius": 1.85 * mm});
            skCircle(sketch, "E29.2.0.2", {"center": v(26.92, 8) * mm, "radius": 1.85 * mm});
            skCircle(sketch, "E29.2.0.3", {"center": v(21.26, 10.34) * mm, "radius": 1.85 * mm});
            skCircle(sketch, "E29.2.0.4", {"center": v(18.92, 16) * mm, "radius": 1.85 * mm});
            skCircle(sketch, "E29.2.0.5", {"center": v(21.26, 21.66) * mm, "radius": 1.85 * mm});
            skCircle(sketch, "E29.2.0.6", {"center": v(26.92, 24) * mm, "radius": 1.85 * mm});
            skCircle(sketch, "E29.2.0.7", {"center": v(32.57, 21.66) * mm, "radius": 1.85 * mm});
            skLineSegment(sketch, "E29.direction1", {"start": v(-29.08, 16) * mm, "end": v(2.92, 16) * mm, "construction": true});
            skCircle(sketch, "E30.1.0.0", {"center": v(-21.08, 16) * mm, "radius": 4 * mm});
            skCircle(sketch, "E30.2.0.0", {"center": v(-5.08, 16) * mm, "radius": 4 * mm});
            skCircle(sketch, "E30.3.0.0", {"center": v(10.92, 16) * mm, "radius": 4 * mm});
            skCircle(sketch, "E30.4.0.0", {"center": v(26.92, 16) * mm, "radius": 4 * mm});
            skLineSegment(sketch, "E30.direction1", {"start": v(-37.08, 16) * mm, "end": v(-21.08, 16) * mm, "construction": true});
            skSolve(sketch);
        }
        {
            var Q0;
            Q0 = qSketchRegion(id + "F2", true);
            extrude(context, id + "F3", {"entities" : qUnion([Q0]), "operationType" : NewBodyOperationType.REMOVE, "oppositeDirection" : true, "depth" : 32 * mm});
        }
        {
            var Q0;
            Q0=makeQuery(id+"F1.opExtrude","SWEPT_FACE",FACE,{"disambiguationData":[OSD([sQuery(id+"F0.wireOp",EDGE,"E0.top")])]});
            var sketch = newSketch(context, id + "F4", { "sketchPlane" : qUnion([Q0])});
            skLineSegment(sketch, "E31.bottom", {"start": v(-57.46, 32) * mm, "end": v(-29.46, 32) * mm});
            skLineSegment(sketch, "E31.top", {"start": v(-57.46, 2) * mm, "end": v(-29.46, 2) * mm});
            skLineSegment(sketch, "E31.left", {"start": v(-57.46, 32) * mm, "end": v(-57.46, 2) * mm});
            skLineSegment(sketch, "E31.right", {"start": v(-29.46, 32) * mm, "end": v(-29.46, 2) * mm});
            skSolve(sketch);
        }
        {
            var Q0;
            Q0 = qSketchRegion(id + "F4", true);
            extrude(context, id + "F5", {"entities" : qUnion([Q0]), "operationType" : NewBodyOperationType.REMOVE, "oppositeDirection" : true, "depth" : 32 * 3 * mm});
        }
        {
            var Q0;
            Q0=makeQuery(id+"F1.opExtrude","SWEPT_FACE",FACE,{"disambiguationData":[OSD([sQuery(id+"F0.wireOp",EDGE,"E6.right")])]});
            var sketch = newSketch(context, id + "F6", { "sketchPlane" : qUnion([Q0])});
            skCircle(sketch, "E32", {"center": v(-66.86, 16) * mm, "radius": 4 * mm});
            skCircle(sketch, "E33", {"center": v(-74.86, 16) * mm, "radius": 1.85 * mm});
            skCircle(sketch, "E34.1.0", {"center": v(-72.52, 10.34) * mm, "radius": 1.85 * mm});
            skCircle(sketch, "E34.2.0", {"center": v(-66.86, 8) * mm, "radius": 1.85 * mm});
            skCircle(sketch, "E34.3.0", {"center": v(-61.2, 10.34) * mm, "radius": 1.85 * mm});
            skCircle(sketch, "E34.4.0", {"center": v(-58.86, 16) * mm, "radius": 1.85 * mm});
            skCircle(sketch, "E34.5.0", {"center": v(-61.2, 21.66) * mm, "radius": 1.85 * mm});
            skCircle(sketch, "E34.6.0", {"center": v(-66.86, 24) * mm, "radius": 1.85 * mm});
            skCircle(sketch, "E34.7.0", {"center": v(-72.52, 21.66) * mm, "radius": 1.85 * mm});
            skCircle(sketch, "E35.1.0.0", {"center": v(-50.86, 16) * mm, "radius": 4 * mm});
            skCircle(sketch, "E35.2.0.0", {"center": v(-34.86, 16) * mm, "radius": 4 * mm});
            skCircle(sketch, "E35.3.0.0", {"center": v(-18.86, 16) * mm, "radius": 4 * mm});
            skCircle(sketch, "E35.4.0.0", {"center": v(-2.86, 16) * mm, "radius": 4 * mm});
            skCircle(sketch, "E35.5.0.0", {"center": v(13.14, 16) * mm, "radius": 4 * mm});
            skCircle(sketch, "E35.6.0.0", {"center": v(29.14, 16) * mm, "radius": 4 * mm});
            skCircle(sketch, "E35.7.0.0", {"center": v(45.14, 16) * mm, "radius": 4 * mm});
            skCircle(sketch, "E35.8.0.0", {"center": v(61.14, 16) * mm, "radius": 4 * mm});
            skCircle(sketch, "E35.9.0.0", {"center": v(77.14, 16) * mm, "radius": 4 * mm});
            skCircle(sketch, "E35.10.0.0", {"center": v(93.14, 16) * mm, "radius": 4 * mm});
            skCircle(sketch, "E35.11.0.0", {"center": v(109.14, 16) * mm, "radius": 4 * mm});
            skCircle(sketch, "E35.12.0.0", {"center": v(125.14, 16) * mm, "radius": 4 * mm});
            skCircle(sketch, "E35.13.0.0", {"center": v(141.14, 16) * mm, "radius": 4 * mm});
            skCircle(sketch, "E35.14.0.0", {"center": v(157.14, 16) * mm, "radius": 4 * mm});
            skCircle(sketch, "E35.15.0.0", {"center": v(173.14, 16) * mm, "radius": 4 * mm});
            skCircle(sketch, "E35.16.0.0", {"center": v(189.14, 16) * mm, "radius": 4 * mm});
            skCircle(sketch, "E35.17.0.0", {"center": v(205.14, 16) * mm, "radius": 4 * mm});
            skCircle(sketch, "E35.18.0.0", {"center": v(221.14, 16) * mm, "radius": 4 * mm});
            skCircle(sketch, "E35.19.0.0", {"center": v(237.14, 16) * mm, "radius": 4 * mm});
            skCircle(sketch, "E35.20.0.0", {"center": v(253.14, 16) * mm, "radius": 4 * mm});
            skCircle(sketch, "E35.21.0.0", {"center": v(269.14, 16) * mm, "radius": 4 * mm});
            skCircle(sketch, "E35.22.0.0", {"center": v(285.14, 16) * mm, "radius": 4 * mm});
            skCircle(sketch, "E35.23.0.0", {"center": v(301.14, 16) * mm, "radius": 4 * mm});
            skCircle(sketch, "E35.24.0.0", {"center": v(317.14, 16) * mm, "radius": 4 * mm});
            skLineSegment(sketch, "E35.direction1", {"start": v(-66.86, 16) * mm, "end": v(-50.86, 16) * mm, "construction": true});
            skCircle(sketch, "E36.1.0.0", {"center": v(-34.86, 8) * mm, "radius": 1.85 * mm});
            skCircle(sketch, "E36.1.0.1", {"center": v(-42.86, 16) * mm, "radius": 1.85 * mm});
            skCircle(sketch, "E36.1.0.2", {"center": v(-34.86, 24) * mm, "radius": 1.85 * mm});
            skCircle(sketch, "E36.1.0.3", {"center": v(-26.86, 16) * mm, "radius": 1.85 * mm});
            skCircle(sketch, "E36.2.0.0", {"center": v(-2.86, 8) * mm, "radius": 1.85 * mm});
            skCircle(sketch, "E36.2.0.1", {"center": v(-10.86, 16) * mm, "radius": 1.85 * mm});
            skCircle(sketch, "E36.2.0.2", {"center": v(-2.86, 24) * mm, "radius": 1.85 * mm});
            skCircle(sketch, "E36.2.0.3", {"center": v(5.14, 16) * mm, "radius": 1.85 * mm});
            skCircle(sketch, "E36.3.0.0", {"center": v(29.14, 8) * mm, "radius": 1.85 * mm});
            skCircle(sketch, "E36.3.0.1", {"center": v(21.14, 16) * mm, "radius": 1.85 * mm});
            skCircle(sketch, "E36.3.0.2", {"center": v(29.14, 24) * mm, "radius": 1.85 * mm});
            skCircle(sketch, "E36.3.0.3", {"center": v(37.14, 16) * mm, "radius": 1.85 * mm});
            skCircle(sketch, "E36.4.0.0", {"center": v(61.14, 8) * mm, "radius": 1.85 * mm});
            skCircle(sketch, "E36.4.0.1", {"center": v(53.14, 16) * mm, "radius": 1.85 * mm});
            skCircle(sketch, "E36.4.0.2", {"center": v(61.14, 24) * mm, "radius": 1.85 * mm});
            skCircle(sketch, "E36.4.0.3", {"center": v(69.14, 16) * mm, "radius": 1.85 * mm});
            skCircle(sketch, "E36.5.0.0", {"center": v(93.14, 8) * mm, "radius": 1.85 * mm});
            skCircle(sketch, "E36.5.0.1", {"center": v(85.14, 16) * mm, "radius": 1.85 * mm});
            skCircle(sketch, "E36.5.0.2", {"center": v(93.14, 24) * mm, "radius": 1.85 * mm});
            skCircle(sketch, "E36.5.0.3", {"center": v(101.14, 16) * mm, "radius": 1.85 * mm});
            skCircle(sketch, "E36.6.0.0", {"center": v(125.14, 8) * mm, "radius": 1.85 * mm});
            skCircle(sketch, "E36.6.0.1", {"center": v(117.14, 16) * mm, "radius": 1.85 * mm});
            skCircle(sketch, "E36.6.0.2", {"center": v(125.14, 24) * mm, "radius": 1.85 * mm});
            skCircle(sketch, "E36.6.0.3", {"center": v(133.14, 16) * mm, "radius": 1.85 * mm});
            skCircle(sketch, "E36.7.0.0", {"center": v(157.14, 8) * mm, "radius": 1.85 * mm});
            skCircle(sketch, "E36.7.0.1", {"center": v(149.14, 16) * mm, "radius": 1.85 * mm});
            skCircle(sketch, "E36.7.0.2", {"center": v(157.14, 24) * mm, "radius": 1.85 * mm});
            skCircle(sketch, "E36.7.0.3", {"center": v(165.14, 16) * mm, "radius": 1.85 * mm});
            skCircle(sketch, "E36.8.0.0", {"center": v(189.14, 8) * mm, "radius": 1.85 * mm});
            skCircle(sketch, "E36.8.0.1", {"center": v(181.14, 16) * mm, "radius": 1.85 * mm});
            skCircle(sketch, "E36.8.0.2", {"center": v(189.14, 24) * mm, "radius": 1.85 * mm});
            skCircle(sketch, "E36.8.0.3", {"center": v(197.14, 16) * mm, "radius": 1.85 * mm});
            skCircle(sketch, "E36.9.0.0", {"center": v(221.14, 8) * mm, "radius": 1.85 * mm});
            skCircle(sketch, "E36.9.0.1", {"center": v(213.14, 16) * mm, "radius": 1.85 * mm});
            skCircle(sketch, "E36.9.0.2", {"center": v(221.14, 24) * mm, "radius": 1.85 * mm});
            skCircle(sketch, "E36.9.0.3", {"center": v(229.14, 16) * mm, "radius": 1.85 * mm});
            skCircle(sketch, "E36.10.0.0", {"center": v(253.14, 8) * mm, "radius": 1.85 * mm});
            skCircle(sketch, "E36.10.0.1", {"center": v(245.14, 16) * mm, "radius": 1.85 * mm});
            skCircle(sketch, "E36.10.0.2", {"center": v(253.14, 24) * mm, "radius": 1.85 * mm});
            skCircle(sketch, "E36.10.0.3", {"center": v(261.14, 16) * mm, "radius": 1.85 * mm});
            skCircle(sketch, "E36.11.0.0", {"center": v(285.14, 8) * mm, "radius": 1.85 * mm});
            skCircle(sketch, "E36.11.0.1", {"center": v(277.14, 16) * mm, "radius": 1.85 * mm});
            skCircle(sketch, "E36.11.0.2", {"center": v(285.14, 24) * mm, "radius": 1.85 * mm});
            skCircle(sketch, "E36.11.0.3", {"center": v(293.14, 16) * mm, "radius": 1.85 * mm});
            skCircle(sketch, "E36.12.0.0", {"center": v(317.14, 8) * mm, "radius": 1.85 * mm});
            skCircle(sketch, "E36.12.0.1", {"center": v(309.14, 16) * mm, "radius": 1.85 * mm});
            skCircle(sketch, "E36.12.0.2", {"center": v(317.14, 24) * mm, "radius": 1.85 * mm});
            skCircle(sketch, "E36.12.0.3", {"center": v(325.14, 16) * mm, "radius": 1.85 * mm});
            skLineSegment(sketch, "E36.direction1", {"start": v(-66.86, 8) * mm, "end": v(-34.86, 8) * mm, "construction": true});
            skCircle(sketch, "E37.1.0.0", {"center": v(2.8, 10.34) * mm, "radius": 1.85 * mm});
            skCircle(sketch, "E37.1.0.1", {"center": v(-8.52, 10.34) * mm, "radius": 1.85 * mm});
            skCircle(sketch, "E37.1.0.2", {"center": v(-8.52, 21.66) * mm, "radius": 1.85 * mm});
            skCircle(sketch, "E37.1.0.3", {"center": v(2.8, 21.66) * mm, "radius": 1.85 * mm});
            skCircle(sketch, "E37.2.0.0", {"center": v(66.8, 10.34) * mm, "radius": 1.85 * mm});
            skCircle(sketch, "E37.2.0.1", {"center": v(55.48, 10.34) * mm, "radius": 1.85 * mm});
            skCircle(sketch, "E37.2.0.2", {"center": v(55.48, 21.66) * mm, "radius": 1.85 * mm});
            skCircle(sketch, "E37.2.0.3", {"center": v(66.8, 21.66) * mm, "radius": 1.85 * mm});
            skCircle(sketch, "E37.3.0.0", {"center": v(130.8, 10.34) * mm, "radius": 1.85 * mm});
            skCircle(sketch, "E37.3.0.1", {"center": v(119.48, 10.34) * mm, "radius": 1.85 * mm});
            skCircle(sketch, "E37.3.0.2", {"center": v(119.48, 21.66) * mm, "radius": 1.85 * mm});
            skCircle(sketch, "E37.3.0.3", {"center": v(130.8, 21.66) * mm, "radius": 1.85 * mm});
            skCircle(sketch, "E37.4.0.0", {"center": v(194.8, 10.34) * mm, "radius": 1.85 * mm});
            skCircle(sketch, "E37.4.0.1", {"center": v(183.48, 10.34) * mm, "radius": 1.85 * mm});
            skCircle(sketch, "E37.4.0.2", {"center": v(183.48, 21.66) * mm, "radius": 1.85 * mm});
            skCircle(sketch, "E37.4.0.3", {"center": v(194.8, 21.66) * mm, "radius": 1.85 * mm});
            skCircle(sketch, "E37.5.0.0", {"center": v(258.8, 10.34) * mm, "radius": 1.85 * mm});
            skCircle(sketch, "E37.5.0.1", {"center": v(247.48, 10.34) * mm, "radius": 1.85 * mm});
            skCircle(sketch, "E37.5.0.2", {"center": v(247.48, 21.66) * mm, "radius": 1.85 * mm});
            skCircle(sketch, "E37.5.0.3", {"center": v(258.8, 21.66) * mm, "radius": 1.85 * mm});
            skCircle(sketch, "E37.6.0.0", {"center": v(322.8, 10.34) * mm, "radius": 1.85 * mm});
            skCircle(sketch, "E37.6.0.1", {"center": v(311.48, 10.34) * mm, "radius": 1.85 * mm});
            skCircle(sketch, "E37.6.0.2", {"center": v(311.48, 21.66) * mm, "radius": 1.85 * mm});
            skCircle(sketch, "E37.6.0.3", {"center": v(322.8, 21.66) * mm, "radius": 1.85 * mm});
            skLineSegment(sketch, "E37.direction1", {"start": v(-61.2, 10.34) * mm, "end": v(2.8, 10.34) * mm, "construction": true});
            skSolve(sketch);
        }
        {
            var Q0;
            Q0 = qSketchRegion(id + "F6", true);
            extrude(context, id + "F7", {"entities" : qUnion([Q0]), "operationType" : NewBodyOperationType.REMOVE, "oppositeDirection" : true, "depth" : 32 * mm});
        }
        {
            var Q0;
            Q0=makeQuery(id+"F1.opExtrude","SWEPT_FACE",FACE,{"disambiguationData":[OSD([sQuery(id+"F0.wireOp",EDGE,"E6.top")])]});
            var sketch = newSketch(context, id + "F8", { "sketchPlane" : qUnion([Q0])});
            skLineSegment(sketch, "E38.bottom", {"start": v(65.23, 32) * mm, "end": v(93.23, 32) * mm});
            skLineSegment(sketch, "E38.top", {"start": v(65.23, 2) * mm, "end": v(93.23, 2) * mm});
            skLineSegment(sketch, "E38.left", {"start": v(65.23, 32) * mm, "end": v(65.23, 2) * mm});
            skLineSegment(sketch, "E38.right", {"start": v(93.23, 32) * mm, "end": v(93.23, 2) * mm});
            skSolve(sketch);
        }
        {
            var Q0;
            Q0 = qSketchRegion(id + "F8", true);
            extrude(context, id + "F9", {"entities" : qUnion([Q0]), "operationType" : NewBodyOperationType.REMOVE, "oppositeDirection" : true, "depth" : 32 * 13 * mm});
        }
        {
            var Q0;
            Q0=makeQuery(id+"F1.opExtrude","SWEPT_FACE",FACE,{"disambiguationData":[OSD([sQuery(id+"F0.wireOp",EDGE,"E12.top")])]});
            var sketch = newSketch(context, id + "F10", { "sketchPlane" : qUnion([Q0])});
            skLineSegment(sketch, "E39.bottom", {"start": v(-191.52, 32) * mm, "end": v(-163.52, 32) * mm});
            skLineSegment(sketch, "E39.top", {"start": v(-191.52, 2) * mm, "end": v(-163.52, 2) * mm});
            skLineSegment(sketch, "E39.left", {"start": v(-191.52, 32) * mm, "end": v(-191.52, 2) * mm});
            skLineSegment(sketch, "E39.right", {"start": v(-163.52, 32) * mm, "end": v(-163.52, 2) * mm});
            skSolve(sketch);
        }
        {
            var Q0;
            Q0 = qSketchRegion(id + "F10", true);
            extrude(context, id + "F11", {"entities" : qUnion([Q0]), "operationType" : NewBodyOperationType.REMOVE, "oppositeDirection" : true, "depth" : 508 * mm});
        }
        {
            var Q0;
            Q0=makeQuery(id+"F1.opExtrude","SWEPT_FACE",FACE,{"disambiguationData":[OSD([sQuery(id+"F0.wireOp",EDGE,"E12.left")])]});
            var sketch = newSketch(context, id + "F12", { "sketchPlane" : qUnion([Q0])});
            skCircle(sketch, "E40", {"center": v(-78.72, 16) * mm, "radius": 4 * mm});
            skCircle(sketch, "E41", {"center": v(-86.72, 16) * mm, "radius": 1.85 * mm});
            skCircle(sketch, "E42.1.0", {"center": v(-84.38, 10.34) * mm, "radius": 1.85 * mm});
            skCircle(sketch, "E42.2.0", {"center": v(-78.72, 8) * mm, "radius": 1.85 * mm});
            skCircle(sketch, "E42.3.0", {"center": v(-73.07, 10.34) * mm, "radius": 1.85 * mm});
            skCircle(sketch, "E42.4.0", {"center": v(-70.72, 16) * mm, "radius": 1.85 * mm});
            skCircle(sketch, "E42.5.0", {"center": v(-73.07, 21.66) * mm, "radius": 1.85 * mm});
            skCircle(sketch, "E42.6.0", {"center": v(-78.72, 24) * mm, "radius": 1.85 * mm});
            skCircle(sketch, "E42.7.0", {"center": v(-84.38, 21.66) * mm, "radius": 1.85 * mm});
            skCircle(sketch, "E43.1.0.1", {"center": v(-46.72, 8) * mm, "radius": 1.85 * mm});
            skCircle(sketch, "E43.1.0.3", {"center": v(-46.72, 16) * mm, "radius": 4 * mm});
            skCircle(sketch, "E43.1.0.4", {"center": v(-54.72, 16) * mm, "radius": 1.85 * mm});
            skCircle(sketch, "E43.1.0.6", {"center": v(-46.72, 24) * mm, "radius": 1.85 * mm});
            skCircle(sketch, "E43.1.0.8", {"center": v(-38.72, 16) * mm, "radius": 1.85 * mm});
            skCircle(sketch, "E43.2.0.0", {"center": v(-9.07, 10.34) * mm, "radius": 1.85 * mm});
            skCircle(sketch, "E43.2.0.1", {"center": v(-14.72, 8) * mm, "radius": 1.85 * mm});
            skCircle(sketch, "E43.2.0.2", {"center": v(-20.38, 10.34) * mm, "radius": 1.85 * mm});
            skCircle(sketch, "E43.2.0.3", {"center": v(-14.72, 16) * mm, "radius": 4 * mm});
            skCircle(sketch, "E43.2.0.4", {"center": v(-22.72, 16) * mm, "radius": 1.85 * mm});
            skCircle(sketch, "E43.2.0.5", {"center": v(-20.38, 21.66) * mm, "radius": 1.85 * mm});
            skCircle(sketch, "E43.2.0.6", {"center": v(-14.72, 24) * mm, "radius": 1.85 * mm});
            skCircle(sketch, "E43.2.0.7", {"center": v(-9.07, 21.66) * mm, "radius": 1.85 * mm});
            skCircle(sketch, "E43.2.0.8", {"center": v(-6.72, 16) * mm, "radius": 1.85 * mm});
            skCircle(sketch, "E43.3.0.1", {"center": v(17.28, 8) * mm, "radius": 1.85 * mm});
            skCircle(sketch, "E43.3.0.3", {"center": v(17.28, 16) * mm, "radius": 4 * mm});
            skCircle(sketch, "E43.3.0.4", {"center": v(9.28, 16) * mm, "radius": 1.85 * mm});
            skCircle(sketch, "E43.3.0.6", {"center": v(17.28, 24) * mm, "radius": 1.85 * mm});
            skCircle(sketch, "E43.3.0.8", {"center": v(25.28, 16) * mm, "radius": 1.85 * mm});
            skCircle(sketch, "E43.4.0.0", {"center": v(54.93, 10.34) * mm, "radius": 1.85 * mm});
            skCircle(sketch, "E43.4.0.1", {"center": v(49.28, 8) * mm, "radius": 1.85 * mm});
            skCircle(sketch, "E43.4.0.2", {"center": v(43.62, 10.34) * mm, "radius": 1.85 * mm});
            skCircle(sketch, "E43.4.0.3", {"center": v(49.28, 16) * mm, "radius": 4 * mm});
            skCircle(sketch, "E43.4.0.4", {"center": v(41.28, 16) * mm, "radius": 1.85 * mm});
            skCircle(sketch, "E43.4.0.5", {"center": v(43.62, 21.66) * mm, "radius": 1.85 * mm});
            skCircle(sketch, "E43.4.0.6", {"center": v(49.28, 24) * mm, "radius": 1.85 * mm});
            skCircle(sketch, "E43.4.0.7", {"center": v(54.93, 21.66) * mm, "radius": 1.85 * mm});
            skCircle(sketch, "E43.4.0.8", {"center": v(57.28, 16) * mm, "radius": 1.85 * mm});
            skLineSegment(sketch, "E43.direction1", {"start": v(-73.07, 10.34) * mm, "end": v(-41.07, 10.34) * mm, "construction": true});
            skCircle(sketch, "E44.1.0.0", {"center": v(-62.72, 16) * mm, "radius": 4 * mm});
            skCircle(sketch, "E44.1.0.1", {"center": v(-30.72, 16) * mm, "radius": 4 * mm});
            skCircle(sketch, "E44.1.0.2", {"center": v(1.28, 16) * mm, "radius": 4 * mm});
            skCircle(sketch, "E44.1.0.3", {"center": v(33.28, 16) * mm, "radius": 4 * mm});
            skLineSegment(sketch, "E44.direction1", {"start": v(-78.72, 16) * mm, "end": v(-62.72, 16) * mm, "construction": true});
            skSolve(sketch);
        }
        {
            var Q0;
            Q0 = qSketchRegion(id + "F12", true);
            extrude(context, id + "F13", {"entities" : qUnion([Q0]), "operationType" : NewBodyOperationType.REMOVE, "oppositeDirection" : true, "depth" : 76.2 * mm});
        }
        {
            var Q0;
            Q0=makeQuery(id+"F1.opExtrude","SWEPT_FACE",FACE,{"disambiguationData":[OSD([sQuery(id+"F0.wireOp",EDGE,"E18.top")])]});
            var sketch = newSketch(context, id + "F14", { "sketchPlane" : qUnion([Q0])});
            skLineSegment(sketch, "E45.bottom", {"start": v(-104.07, 32) * mm, "end": v(-76.07, 32) * mm});
            skLineSegment(sketch, "E45.top", {"start": v(-104.07, 2) * mm, "end": v(-76.07, 2) * mm});
            skLineSegment(sketch, "E45.left", {"start": v(-104.07, 32) * mm, "end": v(-104.07, 2) * mm});
            skLineSegment(sketch, "E45.right", {"start": v(-76.07, 32) * mm, "end": v(-76.07, 2) * mm});
            skSolve(sketch);
        }
        {
            var Q0;
            Q0 = qSketchRegion(id + "F14", true);
            extrude(context, id + "F15", {"entities" : qUnion([Q0]), "operationType" : NewBodyOperationType.REMOVE, "oppositeDirection" : true, "depth" : 304.8 * mm});
        }
        {
            var Q0;
            Q0=makeQuery(id+"F1.opExtrude","SWEPT_FACE",FACE,{"disambiguationData":[OSD([sQuery(id+"F0.wireOp",EDGE,"E18.left")])]});
            var sketch = newSketch(context, id + "F16", { "sketchPlane" : qUnion([Q0])});
            skCircle(sketch, "E46", {"center": v(-379.4, 16) * mm, "radius": 4 * mm});
            skCircle(sketch, "E47", {"center": v(-387.4, 16) * mm, "radius": 1.85 * mm});
            skCircle(sketch, "E48.1.0", {"center": v(-385.06, 10.34) * mm, "radius": 1.85 * mm});
            skCircle(sketch, "E48.2.0", {"center": v(-379.4, 8) * mm, "radius": 1.85 * mm});
            skCircle(sketch, "E48.3.0", {"center": v(-373.74, 10.34) * mm, "radius": 1.85 * mm});
            skCircle(sketch, "E48.4.0", {"center": v(-371.4, 16) * mm, "radius": 1.85 * mm});
            skCircle(sketch, "E48.5.0", {"center": v(-373.74, 21.66) * mm, "radius": 1.85 * mm});
            skCircle(sketch, "E48.6.0", {"center": v(-379.4, 24) * mm, "radius": 1.85 * mm});
            skCircle(sketch, "E48.7.0", {"center": v(-385.06, 21.66) * mm, "radius": 1.85 * mm});
            skCircle(sketch, "E49.1.0.0", {"center": v(-339.4, 16) * mm, "radius": 1.85 * mm});
            skCircle(sketch, "E49.1.0.1", {"center": v(-347.4, 16) * mm, "radius": 4 * mm});
            skCircle(sketch, "E49.1.0.3", {"center": v(-347.4, 8) * mm, "radius": 1.85 * mm});
            skCircle(sketch, "E49.1.0.5", {"center": v(-355.4, 16) * mm, "radius": 1.85 * mm});
            skCircle(sketch, "E49.1.0.7", {"center": v(-347.4, 24) * mm, "radius": 1.85 * mm});
            skCircle(sketch, "E49.2.0.0", {"center": v(-307.4, 16) * mm, "radius": 1.85 * mm});
            skCircle(sketch, "E49.2.0.1", {"center": v(-315.4, 16) * mm, "radius": 4 * mm});
            skCircle(sketch, "E49.2.0.2", {"center": v(-309.74, 10.34) * mm, "radius": 1.85 * mm});
            skCircle(sketch, "E49.2.0.3", {"center": v(-315.4, 8) * mm, "radius": 1.85 * mm});
            skCircle(sketch, "E49.2.0.4", {"center": v(-321.06, 10.34) * mm, "radius": 1.85 * mm});
            skCircle(sketch, "E49.2.0.5", {"center": v(-323.4, 16) * mm, "radius": 1.85 * mm});
            skCircle(sketch, "E49.2.0.6", {"center": v(-321.06, 21.66) * mm, "radius": 1.85 * mm});
            skCircle(sketch, "E49.2.0.7", {"center": v(-315.4, 24) * mm, "radius": 1.85 * mm});
            skCircle(sketch, "E49.2.0.8", {"center": v(-309.74, 21.66) * mm, "radius": 1.85 * mm});
            skCircle(sketch, "E49.3.0.0", {"center": v(-275.4, 16) * mm, "radius": 1.85 * mm});
            skCircle(sketch, "E49.3.0.1", {"center": v(-283.4, 16) * mm, "radius": 4 * mm});
            skCircle(sketch, "E49.3.0.3", {"center": v(-283.4, 8) * mm, "radius": 1.85 * mm});
            skCircle(sketch, "E49.3.0.5", {"center": v(-291.4, 16) * mm, "radius": 1.85 * mm});
            skCircle(sketch, "E49.3.0.7", {"center": v(-283.4, 24) * mm, "radius": 1.85 * mm});
            skCircle(sketch, "E49.4.0.0", {"center": v(-243.4, 16) * mm, "radius": 1.85 * mm});
            skCircle(sketch, "E49.4.0.1", {"center": v(-251.4, 16) * mm, "radius": 4 * mm});
            skCircle(sketch, "E49.4.0.2", {"center": v(-245.74, 10.34) * mm, "radius": 1.85 * mm});
            skCircle(sketch, "E49.4.0.3", {"center": v(-251.4, 8) * mm, "radius": 1.85 * mm});
            skCircle(sketch, "E49.4.0.4", {"center": v(-257.06, 10.34) * mm, "radius": 1.85 * mm});
            skCircle(sketch, "E49.4.0.5", {"center": v(-259.4, 16) * mm, "radius": 1.85 * mm});
            skCircle(sketch, "E49.4.0.6", {"center": v(-257.06, 21.66) * mm, "radius": 1.85 * mm});
            skCircle(sketch, "E49.4.0.7", {"center": v(-251.4, 24) * mm, "radius": 1.85 * mm});
            skCircle(sketch, "E49.4.0.8", {"center": v(-245.74, 21.66) * mm, "radius": 1.85 * mm});
            skCircle(sketch, "E49.5.0.0", {"center": v(-211.4, 16) * mm, "radius": 1.85 * mm});
            skCircle(sketch, "E49.5.0.1", {"center": v(-219.4, 16) * mm, "radius": 4 * mm});
            skCircle(sketch, "E49.5.0.3", {"center": v(-219.4, 8) * mm, "radius": 1.85 * mm});
            skCircle(sketch, "E49.5.0.5", {"center": v(-227.4, 16) * mm, "radius": 1.85 * mm});
            skCircle(sketch, "E49.5.0.7", {"center": v(-219.4, 24) * mm, "radius": 1.85 * mm});
            skCircle(sketch, "E49.6.0.0", {"center": v(-179.4, 16) * mm, "radius": 1.85 * mm});
            skCircle(sketch, "E49.6.0.1", {"center": v(-187.4, 16) * mm, "radius": 4 * mm});
            skCircle(sketch, "E49.6.0.2", {"center": v(-181.74, 10.34) * mm, "radius": 1.85 * mm});
            skCircle(sketch, "E49.6.0.3", {"center": v(-187.4, 8) * mm, "radius": 1.85 * mm});
            skCircle(sketch, "E49.6.0.4", {"center": v(-193.06, 10.34) * mm, "radius": 1.85 * mm});
            skCircle(sketch, "E49.6.0.5", {"center": v(-195.4, 16) * mm, "radius": 1.85 * mm});
            skCircle(sketch, "E49.6.0.6", {"center": v(-193.06, 21.66) * mm, "radius": 1.85 * mm});
            skCircle(sketch, "E49.6.0.7", {"center": v(-187.4, 24) * mm, "radius": 1.85 * mm});
            skCircle(sketch, "E49.6.0.8", {"center": v(-181.74, 21.66) * mm, "radius": 1.85 * mm});
            skLineSegment(sketch, "E49.direction1", {"start": v(-371.4, 16) * mm, "end": v(-339.4, 16) * mm, "construction": true});
            skCircle(sketch, "E50.1.0.0", {"center": v(-363.4, 16) * mm, "radius": 4 * mm});
            skCircle(sketch, "E50.1.0.1", {"center": v(-331.4, 16) * mm, "radius": 4 * mm});
            skCircle(sketch, "E50.1.0.2", {"center": v(-299.4, 16) * mm, "radius": 4 * mm});
            skCircle(sketch, "E50.1.0.3", {"center": v(-267.4, 16) * mm, "radius": 4 * mm});
            skCircle(sketch, "E50.1.0.4", {"center": v(-235.4, 16) * mm, "radius": 4 * mm});
            skCircle(sketch, "E50.1.0.5", {"center": v(-203.4, 16) * mm, "radius": 4 * mm});
            skLineSegment(sketch, "E50.direction1", {"start": v(-379.4, 16) * mm, "end": v(-363.4, 16) * mm, "construction": true});
            skCircle(sketch, "E51.0.7.0", {"center": v(-147.4, 16) * mm, "radius": 1.85 * mm});
            skCircle(sketch, "E51.2.7.0", {"center": v(-155.4, 16) * mm, "radius": 4 * mm});
            skCircle(sketch, "E51.6.7.0", {"center": v(-155.4, 8) * mm, "radius": 1.85 * mm});
            skCircle(sketch, "E51.10.7.0", {"center": v(-163.4, 16) * mm, "radius": 1.85 * mm});
            skCircle(sketch, "E51.14.7.0", {"center": v(-155.4, 24) * mm, "radius": 1.85 * mm});
            skCircle(sketch, "E51.0.8.0", {"center": v(-115.4, 16) * mm, "radius": 1.85 * mm});
            skCircle(sketch, "E51.2.8.0", {"center": v(-123.4, 16) * mm, "radius": 4 * mm});
            skCircle(sketch, "E51.4.8.0", {"center": v(-117.74, 10.34) * mm, "radius": 1.85 * mm});
            skCircle(sketch, "E51.6.8.0", {"center": v(-123.4, 8) * mm, "radius": 1.85 * mm});
            skCircle(sketch, "E51.8.8.0", {"center": v(-129.06, 10.34) * mm, "radius": 1.85 * mm});
            skCircle(sketch, "E51.10.8.0", {"center": v(-131.4, 16) * mm, "radius": 1.85 * mm});
            skCircle(sketch, "E51.12.8.0", {"center": v(-129.06, 21.66) * mm, "radius": 1.85 * mm});
            skCircle(sketch, "E51.14.8.0", {"center": v(-123.4, 24) * mm, "radius": 1.85 * mm});
            skCircle(sketch, "E51.16.8.0", {"center": v(-117.74, 21.66) * mm, "radius": 1.85 * mm});
            skCircle(sketch, "E52.1.0.0", {"center": v(-171.4, 16) * mm, "radius": 4 * mm});
            skCircle(sketch, "E52.1.0.1", {"center": v(-139.4, 16) * mm, "radius": 4 * mm});
            skLineSegment(sketch, "E52.direction1", {"start": v(-187.4, 16) * mm, "end": v(-171.4, 16) * mm, "construction": true});
            skSolve(sketch);
        }
        {
            var Q0;
            Q0 = qSketchRegion(id + "F16", true);
            extrude(context, id + "F17", {"entities" : qUnion([Q0]), "operationType" : NewBodyOperationType.REMOVE, "oppositeDirection" : true, "depth" : 50.8 * mm});
        }
        {
            var Q0;
            Q0=qCreatedBy(makeId("Top.planeOp"),FACE);
            var sketch = newSketch(context, id + "F18", { "sketchPlane" : qUnion([Q0])});
            skLineSegment(sketch, "E53.bottom", {"start": v(-295.52, 214.56) * mm, "end": v(-263.52, 214.56) * mm});
            skLineSegment(sketch, "E53.top", {"start": v(-295.52, 182.56) * mm, "end": v(-263.52, 182.56) * mm});
            skLineSegment(sketch, "E53.left", {"start": v(-295.52, 214.56) * mm, "end": v(-295.52, 182.56) * mm});
            skLineSegment(sketch, "E53.right", {"start": v(-263.52, 214.56) * mm, "end": v(-263.52, 182.56) * mm});
            skCircle(sketch, "E54", {"center": v(-279.52, 198.56) * mm, "radius": 4 * mm});
            skPoint(sketch, "E54.centerSnap0", {"position": v(-279.52, 182.56) * mm});
            skPoint(sketch, "E54.centerSnap1", {"position": v(-295.52, 198.56) * mm});
            skCircle(sketch, "E55", {"center": v(-279.52, 206.56) * mm, "radius": 1.85 * mm});
            skCircle(sketch, "E56.1.0", {"center": v(-285.18, 204.22) * mm, "radius": 1.85 * mm});
            skCircle(sketch, "E56.2.0", {"center": v(-287.52, 198.56) * mm, "radius": 1.85 * mm});
            skCircle(sketch, "E56.3.0", {"center": v(-285.18, 192.9) * mm, "radius": 1.85 * mm});
            skCircle(sketch, "E56.4.0", {"center": v(-279.52, 190.56) * mm, "radius": 1.85 * mm});
            skCircle(sketch, "E56.5.0", {"center": v(-273.87, 192.9) * mm, "radius": 1.85 * mm});
            skCircle(sketch, "E56.6.0", {"center": v(-271.52, 198.56) * mm, "radius": 1.85 * mm});
            skCircle(sketch, "E56.7.0", {"center": v(-273.87, 204.22) * mm, "radius": 1.85 * mm});
            skSolve(sketch);
        }
        {
            var Q0;
            Q0 = qSketchRegion(id + "F18", true);
            extrude(context, id + "F19", {"entities" : qUnion([Q0]), "depth" : 32 * mm});
        }
        {
            var Q0;
            Q0=makeQuery(id+"F19.opExtrude","SWEPT_FACE",FACE,{"disambiguationData":[OSD([sQuery(id+"F18.wireOp",EDGE,"E53.top")])]});
            var sketch = newSketch(context, id + "F20", { "sketchPlane" : qUnion([Q0])});
            skLineSegment(sketch, "E57.bottom", {"start": v(-293.52, 32) * mm, "end": v(-265.52, 32) * mm});
            skLineSegment(sketch, "E57.top", {"start": v(-293.52, 2) * mm, "end": v(-265.52, 2) * mm});
            skLineSegment(sketch, "E57.left", {"start": v(-293.52, 32) * mm, "end": v(-293.52, 2) * mm});
            skLineSegment(sketch, "E57.right", {"start": v(-265.52, 32) * mm, "end": v(-265.52, 2) * mm});
            skSolve(sketch);
        }
        {
            var Q0;
            Q0 = qSketchRegion(id + "F20", true);
            extrude(context, id + "F21", {"entities" : qUnion([Q0]), "operationType" : NewBodyOperationType.REMOVE, "oppositeDirection" : true, "depth" : 304.8 * mm});
        }
        {
            var Q0;
            Q0=makeQuery(id+"F19.opExtrude","SWEPT_FACE",FACE,{"disambiguationData":[OSD([sQuery(id+"F18.wireOp",EDGE,"E53.left")])]});
            var sketch = newSketch(context, id + "F22", { "sketchPlane" : qUnion([Q0])});
            skCircle(sketch, "E58", {"center": v(-198.56, 16) * mm, "radius": 4 * mm});
            skPoint(sketch, "E58.centerSnap0", {"position": v(-214.56, 16) * mm});
            skPoint(sketch, "E58.centerSnap1", {"position": v(-198.56, 0) * mm});
            skCircle(sketch, "E59", {"center": v(-206.56, 16) * mm, "radius": 1.85 * mm});
            skCircle(sketch, "E60.1.0", {"center": v(-204.22, 10.34) * mm, "radius": 1.85 * mm});
            skCircle(sketch, "E60.2.0", {"center": v(-198.56, 8) * mm, "radius": 1.85 * mm});
            skCircle(sketch, "E60.3.0", {"center": v(-192.9, 10.34) * mm, "radius": 1.85 * mm});
            skCircle(sketch, "E60.4.0", {"center": v(-190.56, 16) * mm, "radius": 1.85 * mm});
            skCircle(sketch, "E60.5.0", {"center": v(-192.9, 21.66) * mm, "radius": 1.85 * mm});
            skCircle(sketch, "E60.6.0", {"center": v(-198.56, 24) * mm, "radius": 1.85 * mm});
            skCircle(sketch, "E60.7.0", {"center": v(-204.22, 21.66) * mm, "radius": 1.85 * mm});
            skSolve(sketch);
        }
        {
            var Q0;
            Q0 = qSketchRegion(id + "F22", true);
            extrude(context, id + "F23", {"entities" : qUnion([Q0]), "operationType" : NewBodyOperationType.REMOVE, "oppositeDirection" : true, "depth" : 127 * mm});
        }
        {
            var Q0;
            Q0=makeQuery(id+"F1.opExtrude","CAP_EDGE",EDGE,{"disambiguationData":[OSD([sQuery(id+"F0.wireOp",EDGE,"E0.left")])],"isStart":true});
            var Q1;
            Q1=makeQuery(id+"F1.opExtrude","CAP_EDGE",EDGE,{"disambiguationData":[OSD([sQuery(id+"F0.wireOp",EDGE,"E0.right")])],"isStart":true});
            var Q2;
            {var subQ0=sQuery(id+"F0.wireOp",EDGE,"E0.right");var subQ1=sQuery(id+"F0.wireOp",EDGE,"E0.top");Q2=makeQuery(id+"F5.boolean.opBoolean","SPLIT",EDGE,{"disambiguationData":[TD([makeQuery(id+"F1.opExtrude","SWEPT_FACE",FACE,{"disambiguationData":[OSD([subQ0])]})])],"derivedFrom":makeQuery(id+"F1.opExtrude","CAP_EDGE",EDGE,{"disambiguationData":[OSD([subQ1])],"isStart":false})});}
            var Q3;
            {var subQ0=sQuery(id+"F0.wireOp",EDGE,"E0.left");var subQ1=sQuery(id+"F0.wireOp",EDGE,"E0.top");Q3=makeQuery(id+"F5.boolean.opBoolean","SPLIT",EDGE,{"disambiguationData":[TD([makeQuery(id+"F1.opExtrude","SWEPT_FACE",FACE,{"disambiguationData":[OSD([subQ0])]})])],"derivedFrom":makeQuery(id+"F1.opExtrude","CAP_EDGE",EDGE,{"disambiguationData":[OSD([subQ1])],"isStart":false})});}
            var Q4;
            {var subQ0=sQuery(id+"F0.wireOp",EDGE,"E0.bottom");var subQ1=sQuery(id+"F0.wireOp",EDGE,"E0.right");Q4=makeQuery(id+"F5.boolean.opBoolean","SPLIT",EDGE,{"disambiguationData":[TD([makeQuery(id+"F1.opExtrude","SWEPT_FACE",FACE,{"disambiguationData":[OSD([subQ1])]})])],"derivedFrom":makeQuery(id+"F1.opExtrude","CAP_EDGE",EDGE,{"disambiguationData":[OSD([subQ0])],"isStart":false})});}
            var Q5;
            {var subQ0=sQuery(id+"F0.wireOp",EDGE,"E0.bottom");var subQ1=sQuery(id+"F0.wireOp",EDGE,"E0.left");Q5=makeQuery(id+"F5.boolean.opBoolean","SPLIT",EDGE,{"disambiguationData":[TD([makeQuery(id+"F1.opExtrude","SWEPT_FACE",FACE,{"disambiguationData":[OSD([subQ1])]})])],"derivedFrom":makeQuery(id+"F1.opExtrude","CAP_EDGE",EDGE,{"disambiguationData":[OSD([subQ0])],"isStart":false})});}
            var Q6;
            {var subQ0=sQuery(id+"F0.wireOp",EDGE,"E6.left");var subQ1=sQuery(id+"F0.wireOp",EDGE,"E6.top");Q6=makeQuery(id+"F9.boolean.opBoolean","SPLIT",EDGE,{"disambiguationData":[TD([makeQuery(id+"F1.opExtrude","SWEPT_FACE",FACE,{"disambiguationData":[OSD([subQ0])]})])],"derivedFrom":makeQuery(id+"F1.opExtrude","CAP_EDGE",EDGE,{"disambiguationData":[OSD([subQ1])],"isStart":false})});}
            var Q7;
            {var subQ0=sQuery(id+"F0.wireOp",EDGE,"E6.right");var subQ1=sQuery(id+"F0.wireOp",EDGE,"E6.top");Q7=makeQuery(id+"F9.boolean.opBoolean","SPLIT",EDGE,{"disambiguationData":[TD([makeQuery(id+"F1.opExtrude","SWEPT_FACE",FACE,{"disambiguationData":[OSD([subQ0])]})])],"derivedFrom":makeQuery(id+"F1.opExtrude","CAP_EDGE",EDGE,{"disambiguationData":[OSD([subQ1])],"isStart":false})});}
            var Q8;
            Q8=makeQuery(id+"F1.opExtrude","CAP_EDGE",EDGE,{"disambiguationData":[OSD([sQuery(id+"F0.wireOp",EDGE,"E6.right")])],"isStart":true});
            var Q9;
            Q9=makeQuery(id+"F1.opExtrude","CAP_EDGE",EDGE,{"disambiguationData":[OSD([sQuery(id+"F0.wireOp",EDGE,"E6.left")])],"isStart":true});
            var Q10;
            {var subQ0=sQuery(id+"F0.wireOp",EDGE,"E6.bottom");var subQ1=sQuery(id+"F0.wireOp",EDGE,"E6.right");Q10=makeQuery(id+"F9.boolean.opBoolean","SPLIT",EDGE,{"disambiguationData":[TD([makeQuery(id+"F1.opExtrude","SWEPT_FACE",FACE,{"disambiguationData":[OSD([subQ1])]})])],"derivedFrom":makeQuery(id+"F1.opExtrude","CAP_EDGE",EDGE,{"disambiguationData":[OSD([subQ0])],"isStart":false})});}
            var Q11;
            {var subQ0=sQuery(id+"F0.wireOp",EDGE,"E6.bottom");var subQ1=sQuery(id+"F0.wireOp",EDGE,"E6.left");Q11=makeQuery(id+"F9.boolean.opBoolean","SPLIT",EDGE,{"disambiguationData":[TD([makeQuery(id+"F1.opExtrude","SWEPT_FACE",FACE,{"disambiguationData":[OSD([subQ1])]})])],"derivedFrom":makeQuery(id+"F1.opExtrude","CAP_EDGE",EDGE,{"disambiguationData":[OSD([subQ0])],"isStart":false})});}
            var Q12;
            {var subQ0=sQuery(id+"F0.wireOp",EDGE,"E12.right");var subQ1=sQuery(id+"F0.wireOp",EDGE,"E12.top");Q12=makeQuery(id+"F11.boolean.opBoolean","SPLIT",EDGE,{"disambiguationData":[TD([makeQuery(id+"F1.opExtrude","SWEPT_FACE",FACE,{"disambiguationData":[OSD([subQ0])]})])],"derivedFrom":makeQuery(id+"F1.opExtrude","CAP_EDGE",EDGE,{"disambiguationData":[OSD([subQ1])],"isStart":false})});}
            var Q13;
            {var subQ0=sQuery(id+"F0.wireOp",EDGE,"E12.left");var subQ1=sQuery(id+"F0.wireOp",EDGE,"E12.top");Q13=makeQuery(id+"F11.boolean.opBoolean","SPLIT",EDGE,{"disambiguationData":[TD([makeQuery(id+"F1.opExtrude","SWEPT_FACE",FACE,{"disambiguationData":[OSD([subQ0])]})])],"derivedFrom":makeQuery(id+"F1.opExtrude","CAP_EDGE",EDGE,{"disambiguationData":[OSD([subQ1])],"isStart":false})});}
            var Q14;
            Q14=makeQuery(id+"F1.opExtrude","CAP_EDGE",EDGE,{"disambiguationData":[OSD([sQuery(id+"F0.wireOp",EDGE,"E12.right")])],"isStart":true});
            var Q15;
            Q15=makeQuery(id+"F1.opExtrude","CAP_EDGE",EDGE,{"disambiguationData":[OSD([sQuery(id+"F0.wireOp",EDGE,"E12.left")])],"isStart":true});
            var Q16;
            {var subQ0=sQuery(id+"F0.wireOp",EDGE,"E12.bottom");var subQ1=sQuery(id+"F0.wireOp",EDGE,"E12.right");Q16=makeQuery(id+"F11.boolean.opBoolean","SPLIT",EDGE,{"disambiguationData":[TD([makeQuery(id+"F1.opExtrude","SWEPT_FACE",FACE,{"disambiguationData":[OSD([subQ1])]})])],"derivedFrom":makeQuery(id+"F1.opExtrude","CAP_EDGE",EDGE,{"disambiguationData":[OSD([subQ0])],"isStart":false})});}
            var Q17;
            {var subQ0=sQuery(id+"F0.wireOp",EDGE,"E12.bottom");var subQ1=sQuery(id+"F0.wireOp",EDGE,"E12.left");Q17=makeQuery(id+"F11.boolean.opBoolean","SPLIT",EDGE,{"disambiguationData":[TD([makeQuery(id+"F1.opExtrude","SWEPT_FACE",FACE,{"disambiguationData":[OSD([subQ1])]})])],"derivedFrom":makeQuery(id+"F1.opExtrude","CAP_EDGE",EDGE,{"disambiguationData":[OSD([subQ0])],"isStart":false})});}
            var Q18;
            {var subQ0=sQuery(id+"F0.wireOp",EDGE,"E18.left");var subQ1=sQuery(id+"F0.wireOp",EDGE,"E18.top");Q18=makeQuery(id+"F15.boolean.opBoolean","SPLIT",EDGE,{"disambiguationData":[TD([makeQuery(id+"F1.opExtrude","SWEPT_FACE",FACE,{"disambiguationData":[OSD([subQ0])]})])],"derivedFrom":makeQuery(id+"F1.opExtrude","CAP_EDGE",EDGE,{"disambiguationData":[OSD([subQ1])],"isStart":false})});}
            var Q19;
            {var subQ0=sQuery(id+"F0.wireOp",EDGE,"E18.right");var subQ1=sQuery(id+"F0.wireOp",EDGE,"E18.top");Q19=makeQuery(id+"F15.boolean.opBoolean","SPLIT",EDGE,{"disambiguationData":[TD([makeQuery(id+"F1.opExtrude","SWEPT_FACE",FACE,{"disambiguationData":[OSD([subQ0])]})])],"derivedFrom":makeQuery(id+"F1.opExtrude","CAP_EDGE",EDGE,{"disambiguationData":[OSD([subQ1])],"isStart":false})});}
            var Q20;
            Q20=makeQuery(id+"F1.opExtrude","CAP_EDGE",EDGE,{"disambiguationData":[OSD([sQuery(id+"F0.wireOp",EDGE,"E18.left")])],"isStart":true});
            var Q21;
            Q21=makeQuery(id+"F1.opExtrude","CAP_EDGE",EDGE,{"disambiguationData":[OSD([sQuery(id+"F0.wireOp",EDGE,"E18.right")])],"isStart":true});
            var Q22;
            {var subQ0=sQuery(id+"F0.wireOp",EDGE,"E18.bottom");var subQ1=sQuery(id+"F0.wireOp",EDGE,"E18.right");Q22=makeQuery(id+"F15.boolean.opBoolean","SPLIT",EDGE,{"disambiguationData":[TD([makeQuery(id+"F1.opExtrude","SWEPT_FACE",FACE,{"disambiguationData":[OSD([subQ1])]})])],"derivedFrom":makeQuery(id+"F1.opExtrude","CAP_EDGE",EDGE,{"disambiguationData":[OSD([subQ0])],"isStart":false})});}
            var Q23;
            {var subQ0=sQuery(id+"F0.wireOp",EDGE,"E18.bottom");var subQ1=sQuery(id+"F0.wireOp",EDGE,"E18.left");Q23=makeQuery(id+"F15.boolean.opBoolean","SPLIT",EDGE,{"disambiguationData":[TD([makeQuery(id+"F1.opExtrude","SWEPT_FACE",FACE,{"disambiguationData":[OSD([subQ1])]})])],"derivedFrom":makeQuery(id+"F1.opExtrude","CAP_EDGE",EDGE,{"disambiguationData":[OSD([subQ0])],"isStart":false})});}
            var Q24;
            Q24=makeQuery(id+"F19.opExtrude","CAP_EDGE",EDGE,{"disambiguationData":[OSD([sQuery(id+"F18.wireOp",EDGE,"E53.left")])],"isStart":true});
            var Q25;
            Q25=makeQuery(id+"F19.opExtrude","CAP_EDGE",EDGE,{"disambiguationData":[OSD([sQuery(id+"F18.wireOp",EDGE,"E53.right")])],"isStart":true});
            var Q26;
            {var subQ0=sQuery(id+"F18.wireOp",EDGE,"E53.bottom");var subQ1=sQuery(id+"F18.wireOp",EDGE,"E53.left");Q26=makeQuery(id+"F21.boolean.opBoolean","SPLIT",EDGE,{"disambiguationData":[TD([makeQuery(id+"F19.opExtrude","SWEPT_FACE",FACE,{"disambiguationData":[OSD([subQ1])]})])],"derivedFrom":makeQuery(id+"F19.opExtrude","CAP_EDGE",EDGE,{"disambiguationData":[OSD([subQ0])],"isStart":false})});}
            var Q27;
            {var subQ0=sQuery(id+"F18.wireOp",EDGE,"E53.bottom");var subQ1=sQuery(id+"F18.wireOp",EDGE,"E53.right");Q27=makeQuery(id+"F21.boolean.opBoolean","SPLIT",EDGE,{"disambiguationData":[TD([makeQuery(id+"F19.opExtrude","SWEPT_FACE",FACE,{"disambiguationData":[OSD([subQ1])]})])],"derivedFrom":makeQuery(id+"F19.opExtrude","CAP_EDGE",EDGE,{"disambiguationData":[OSD([subQ0])],"isStart":false})});}
            var Q28;
            {var subQ0=sQuery(id+"F18.wireOp",EDGE,"E53.right");var subQ1=sQuery(id+"F18.wireOp",EDGE,"E53.top");Q28=makeQuery(id+"F21.boolean.opBoolean","SPLIT",EDGE,{"disambiguationData":[TD([makeQuery(id+"F19.opExtrude","SWEPT_FACE",FACE,{"disambiguationData":[OSD([subQ0])]})])],"derivedFrom":makeQuery(id+"F19.opExtrude","CAP_EDGE",EDGE,{"disambiguationData":[OSD([subQ1])],"isStart":false})});}
            var Q29;
            {var subQ0=sQuery(id+"F18.wireOp",EDGE,"E53.left");var subQ1=sQuery(id+"F18.wireOp",EDGE,"E53.top");Q29=makeQuery(id+"F21.boolean.opBoolean","SPLIT",EDGE,{"disambiguationData":[TD([makeQuery(id+"F19.opExtrude","SWEPT_FACE",FACE,{"disambiguationData":[OSD([subQ0])]})])],"derivedFrom":makeQuery(id+"F19.opExtrude","CAP_EDGE",EDGE,{"disambiguationData":[OSD([subQ1])],"isStart":false})});}
            fillet(context, id + "F24", {"entities" : qUnion([Q0, Q1, Q2, Q3, Q4, Q5, Q6, Q7, Q8, Q9, Q10, Q11, Q12, Q13, Q14, Q15, Q16, Q17, Q18, Q19, Q20, Q21, Q22, Q23, Q24, Q25, Q26, Q27, Q28, Q29]), "radius" : 2 * mm, "tangentPropagation" : true, "allowEdgeOverflow" : false});
        }
    });
